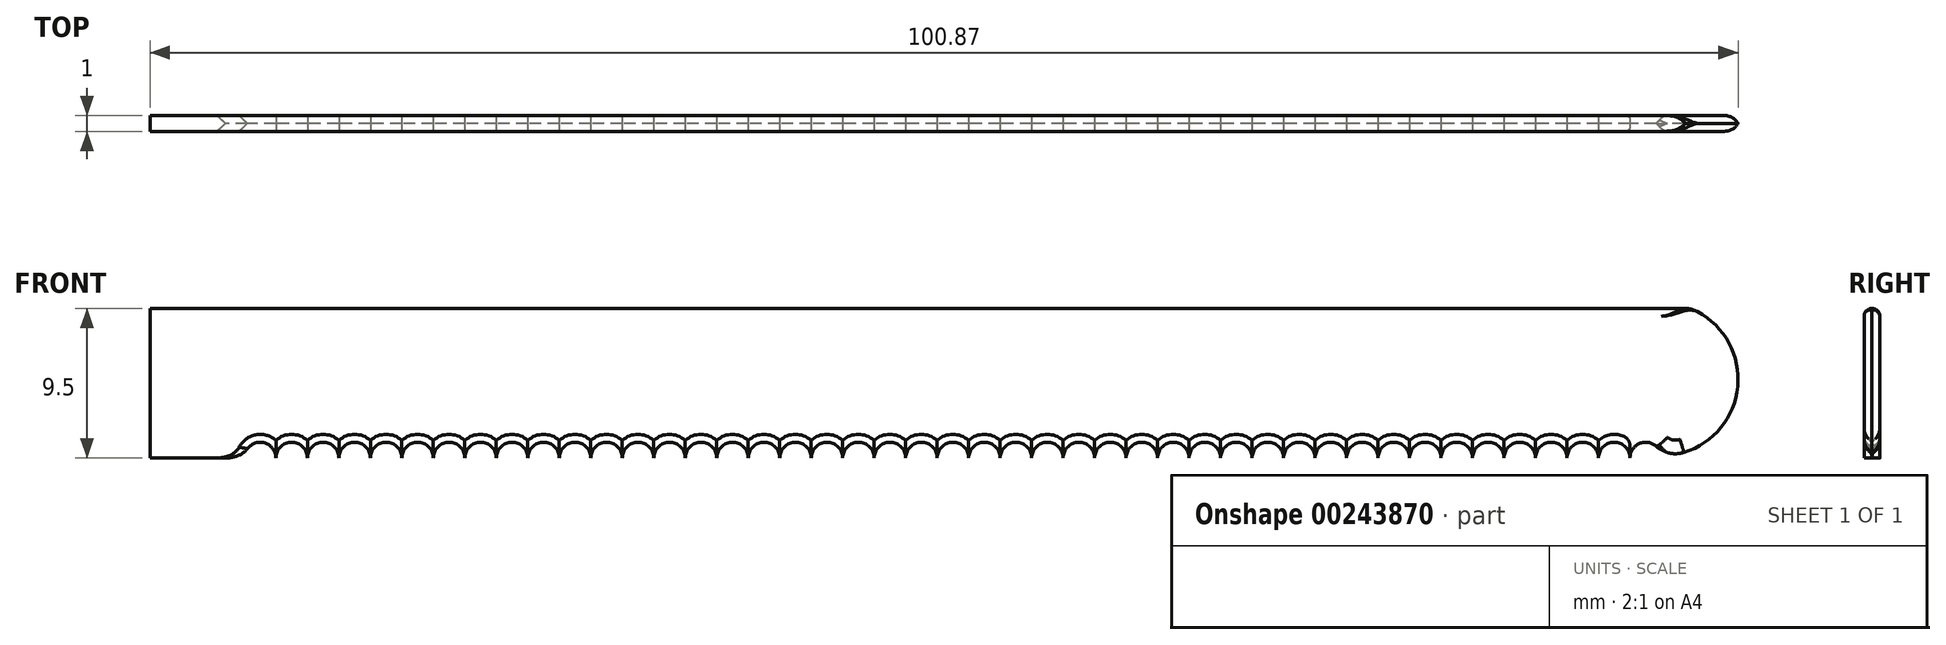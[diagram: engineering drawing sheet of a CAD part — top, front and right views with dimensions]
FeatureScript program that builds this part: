
annotation { "Feature Type Name" : "Feature", "Feature Type Description" : "" }
export const myFeature = defineFeature(function(context is Context, id is Id, definition is map)
    precondition{}
    {
        {
            var Q0;
            Q0=qCreatedBy(makeId("Front.planeOp"),FACE);
            var sketch = newSketch(context, id + "F0", { "sketchPlane" : qUnion([Q0])});
            skLineSegment(sketch, "E0.top", {"start": v(30, 10) * mm, "end": v(-60, 10) * mm});
            skLineSegment(sketch, "E0.right", {"start": v(-60, 0) * mm, "end": v(-60, 10) * mm});
            skLineSegment(sketch, "E1", {"start": v(-60, 0) * mm, "end": v(-58, 0) * mm});
            skLineSegment(sketch, "E2", {"start": v(-58, 0) * mm, "end": v(-56, 0) * mm});
            skLineSegment(sketch, "E3", {"start": v(-56, 0) * mm, "end": v(-54, 0) * mm});
            skLineSegment(sketch, "E4.bottom", {"start": v(-60, 10) * mm, "end": v(-66, 10) * mm});
            skLineSegment(sketch, "E4.top", {"start": v(-60, 0) * mm, "end": v(-66, 0) * mm});
            skLineSegment(sketch, "E4.left", {"start": v(-60, 10) * mm, "end": v(-60, 0) * mm});
            skLineSegment(sketch, "E4.right", {"start": v(-66, 10) * mm, "end": v(-66, 0) * mm});
            skArc(sketch, "E5", {"start": v(-58, 0) * mm, "mid": v(-59, 1) * mm, "end": v(-60, 0) * mm});
            skArc(sketch, "E6", {"start": v(-56, 0) * mm, "mid": v(-57, 1) * mm, "end": v(-58, 0) * mm});
            skArc(sketch, "E7", {"start": v(-54, 0) * mm, "mid": v(-55, 1) * mm, "end": v(-56, 0) * mm});
            skLineSegment(sketch, "E8", {"start": v(-54, 0) * mm, "end": v(-52, 0) * mm});
            skLineSegment(sketch, "E9", {"start": v(-52, 0) * mm, "end": v(-50, 0) * mm});
            skLineSegment(sketch, "E10", {"start": v(-50, 0) * mm, "end": v(-48, 0) * mm});
            skLineSegment(sketch, "E11", {"start": v(-48, 0) * mm, "end": v(-46, 0) * mm});
            skLineSegment(sketch, "E12", {"start": v(-46, 0) * mm, "end": v(-44, 0) * mm});
            skLineSegment(sketch, "E13", {"start": v(-44, 0) * mm, "end": v(-42, 0) * mm});
            skLineSegment(sketch, "E14", {"start": v(-42, 0) * mm, "end": v(-40, 0) * mm});
            skLineSegment(sketch, "E15", {"start": v(-40, 0) * mm, "end": v(-38, 0) * mm});
            skLineSegment(sketch, "E16", {"start": v(-38, 0) * mm, "end": v(-36, 0) * mm});
            skLineSegment(sketch, "E17", {"start": v(-36, 0) * mm, "end": v(-34, 0) * mm});
            skLineSegment(sketch, "E18", {"start": v(-34, 0) * mm, "end": v(-32, 0) * mm});
            skLineSegment(sketch, "E19", {"start": v(-32, 0) * mm, "end": v(-30, 0) * mm});
            skLineSegment(sketch, "E20", {"start": v(-30, 0) * mm, "end": v(-28, 0) * mm});
            skLineSegment(sketch, "E21", {"start": v(-28, 0) * mm, "end": v(-26, 0) * mm});
            skLineSegment(sketch, "E22", {"start": v(-26, 0) * mm, "end": v(-24, 0) * mm});
            skLineSegment(sketch, "E23", {"start": v(-24, 0) * mm, "end": v(-22, 0) * mm});
            skLineSegment(sketch, "E24", {"start": v(-22, 0) * mm, "end": v(-20, 0) * mm});
            skLineSegment(sketch, "E25", {"start": v(-20, 0) * mm, "end": v(-18, 0) * mm});
            skLineSegment(sketch, "E26", {"start": v(-18, 0) * mm, "end": v(-16, 0) * mm});
            skLineSegment(sketch, "E27", {"start": v(-16, 0) * mm, "end": v(-14, 0) * mm});
            skLineSegment(sketch, "E28", {"start": v(-14, 0) * mm, "end": v(-12, 0) * mm});
            skLineSegment(sketch, "E29", {"start": v(-12, 0) * mm, "end": v(-10, 0) * mm});
            skLineSegment(sketch, "E30", {"start": v(-10, 0) * mm, "end": v(-8, 0) * mm});
            skLineSegment(sketch, "E31", {"start": v(-8, 0) * mm, "end": v(-6, 0) * mm});
            skLineSegment(sketch, "E32", {"start": v(-6, 0) * mm, "end": v(-4, 0) * mm});
            skLineSegment(sketch, "E33", {"start": v(-4, 0) * mm, "end": v(-2, 0) * mm});
            skLineSegment(sketch, "E34", {"start": v(-2, 0) * mm, "end": v(0, 0) * mm});
            skArc(sketch, "E35", {"start": v(-52, 0) * mm, "mid": v(-53, 1) * mm, "end": v(-54, 0) * mm});
            skArc(sketch, "E36", {"start": v(-50, 0) * mm, "mid": v(-51, 1) * mm, "end": v(-52, 0) * mm});
            skArc(sketch, "E37", {"start": v(-48, 0) * mm, "mid": v(-49, 1) * mm, "end": v(-50, 0) * mm});
            skArc(sketch, "E38", {"start": v(-46, 0) * mm, "mid": v(-47, 1) * mm, "end": v(-48, 0) * mm});
            skArc(sketch, "E39", {"start": v(-44, 0) * mm, "mid": v(-45, 1) * mm, "end": v(-46, 0) * mm});
            skArc(sketch, "E40", {"start": v(-42, 0) * mm, "mid": v(-43, 1) * mm, "end": v(-44, 0) * mm});
            skArc(sketch, "E41", {"start": v(-40, 0) * mm, "mid": v(-41, 1) * mm, "end": v(-42, 0) * mm});
            skArc(sketch, "E42", {"start": v(-38, 0) * mm, "mid": v(-39, 1) * mm, "end": v(-40, 0) * mm});
            skArc(sketch, "E43", {"start": v(-36, 0) * mm, "mid": v(-37, 1) * mm, "end": v(-38, 0) * mm});
            skArc(sketch, "E44", {"start": v(-34, 0) * mm, "mid": v(-35, 1) * mm, "end": v(-36, 0) * mm});
            skArc(sketch, "E45", {"start": v(-32, 0) * mm, "mid": v(-33, 1) * mm, "end": v(-34, 0) * mm});
            skArc(sketch, "E46", {"start": v(-30, 0) * mm, "mid": v(-31, 1) * mm, "end": v(-32, 0) * mm});
            skArc(sketch, "E47", {"start": v(-28, 0) * mm, "mid": v(-29, 1) * mm, "end": v(-30, 0) * mm});
            skArc(sketch, "E48", {"start": v(-26, 0) * mm, "mid": v(-27, 1) * mm, "end": v(-28, 0) * mm});
            skArc(sketch, "E49", {"start": v(-24, 0) * mm, "mid": v(-25, 1) * mm, "end": v(-26, 0) * mm});
            skArc(sketch, "E50", {"start": v(-22, 0) * mm, "mid": v(-23, 1) * mm, "end": v(-24, 0) * mm});
            skArc(sketch, "E51", {"start": v(-20, 0) * mm, "mid": v(-21, 1) * mm, "end": v(-22, 0) * mm});
            skArc(sketch, "E52", {"start": v(-18, 0) * mm, "mid": v(-19, 1) * mm, "end": v(-20, 0) * mm});
            skArc(sketch, "E53", {"start": v(-16, 0) * mm, "mid": v(-17, 1) * mm, "end": v(-18, 0) * mm});
            skArc(sketch, "E54", {"start": v(-14, 0) * mm, "mid": v(-15, 1) * mm, "end": v(-16, 0) * mm});
            skArc(sketch, "E55", {"start": v(-12, 0) * mm, "mid": v(-13, 1) * mm, "end": v(-14, 0) * mm});
            skArc(sketch, "E56", {"start": v(-10, 0) * mm, "mid": v(-11, 1) * mm, "end": v(-12, 0) * mm});
            skArc(sketch, "E57", {"start": v(-8, 0) * mm, "mid": v(-9, 1) * mm, "end": v(-10, 0) * mm});
            skArc(sketch, "E58", {"start": v(-6, 0) * mm, "mid": v(-7, 1) * mm, "end": v(-8, 0) * mm});
            skArc(sketch, "E59", {"start": v(-4, 0) * mm, "mid": v(-5, 1) * mm, "end": v(-6, 0) * mm});
            skArc(sketch, "E60", {"start": v(-2, 0) * mm, "mid": v(-3, 1) * mm, "end": v(-4, 0) * mm});
            skArc(sketch, "E61", {"start": v(0, 0) * mm, "mid": v(-1, 1) * mm, "end": v(-2, 0) * mm});
            skLineSegment(sketch, "E62", {"start": v(30, 10) * mm, "end": v(30, 0) * mm});
            skLineSegment(sketch, "E63", {"start": v(0, 0) * mm, "end": v(2, 0) * mm});
            skLineSegment(sketch, "E64", {"start": v(2, 0) * mm, "end": v(4, 0) * mm});
            skLineSegment(sketch, "E65", {"start": v(4, 0) * mm, "end": v(6, 0) * mm});
            skLineSegment(sketch, "E66", {"start": v(6, 0) * mm, "end": v(8, 0) * mm});
            skLineSegment(sketch, "E67", {"start": v(8, 0) * mm, "end": v(10, 0) * mm});
            skLineSegment(sketch, "E68", {"start": v(10, 0) * mm, "end": v(12, 0) * mm});
            skLineSegment(sketch, "E69", {"start": v(12, 0) * mm, "end": v(14, 0) * mm});
            skLineSegment(sketch, "E70", {"start": v(14, 0) * mm, "end": v(16, 0) * mm});
            skLineSegment(sketch, "E71", {"start": v(16, 0) * mm, "end": v(18, 0) * mm});
            skLineSegment(sketch, "E72", {"start": v(18, 0) * mm, "end": v(20, 0) * mm});
            skLineSegment(sketch, "E73", {"start": v(20, 0) * mm, "end": v(22, 0) * mm});
            skLineSegment(sketch, "E74", {"start": v(22, 0) * mm, "end": v(24, 0) * mm});
            skLineSegment(sketch, "E75", {"start": v(24, 0) * mm, "end": v(26, 0) * mm});
            skLineSegment(sketch, "E76", {"start": v(26, 0) * mm, "end": v(28, 0) * mm});
            skLineSegment(sketch, "E77", {"start": v(28, 0) * mm, "end": v(30, 0) * mm});
            skArc(sketch, "E78", {"start": v(2, 0) * mm, "mid": v(1, 1) * mm, "end": v(0, 0) * mm});
            skArc(sketch, "E79", {"start": v(4, 0) * mm, "mid": v(3, 1) * mm, "end": v(2, 0) * mm});
            skArc(sketch, "E80", {"start": v(6, 0) * mm, "mid": v(5, 1) * mm, "end": v(4, 0) * mm});
            skArc(sketch, "E81", {"start": v(8, 0) * mm, "mid": v(7, 1) * mm, "end": v(6, 0) * mm});
            skArc(sketch, "E82", {"start": v(10, 0) * mm, "mid": v(9, 1) * mm, "end": v(8, 0) * mm});
            skArc(sketch, "E83", {"start": v(12, 0) * mm, "mid": v(11, 1) * mm, "end": v(10, 0) * mm});
            skArc(sketch, "E84", {"start": v(14, 0) * mm, "mid": v(13, 1) * mm, "end": v(12, 0) * mm});
            skArc(sketch, "E85", {"start": v(16, 0) * mm, "mid": v(15, 1) * mm, "end": v(14, 0) * mm});
            skArc(sketch, "E86", {"start": v(18, 0) * mm, "mid": v(17, 1) * mm, "end": v(16, 0) * mm});
            skArc(sketch, "E87", {"start": v(20, 0) * mm, "mid": v(19, 1) * mm, "end": v(18, 0) * mm});
            skArc(sketch, "E88", {"start": v(22, 0) * mm, "mid": v(21, 1) * mm, "end": v(20, 0) * mm});
            skArc(sketch, "E89", {"start": v(24, 0) * mm, "mid": v(23, 1) * mm, "end": v(22, 0) * mm});
            skArc(sketch, "E90", {"start": v(26, 0) * mm, "mid": v(25, 1) * mm, "end": v(24, 0) * mm});
            skArc(sketch, "E91", {"start": v(28, 0) * mm, "mid": v(27, 1) * mm, "end": v(26, 0) * mm});
            skArc(sketch, "E92", {"start": v(30, 0) * mm, "mid": v(29, 1) * mm, "end": v(28, 0) * mm});
            skArc(sketch, "E93", {"start": v(30, 0) * mm, "mid": v(35, 5) * mm, "end": v(30, 10) * mm});
            skSolve(sketch);
        }
        {
            var Q0;
            Q0=makeQuery(id+"F0.imprint","IMPRINT",FACE,{"disambiguationData":[TD([[makeQuery(id+"F0.imprint","IMPRINT",EDGE,{"derivedFrom":sQuery(id+"F0.wireOp",EDGE,"E4.bottom")}),1.0]])]});
            var Q1;
            Q1=makeQuery(id+"F0.imprint","IMPRINT",FACE,{"disambiguationData":[TD([[makeQuery(id+"F0.imprint","IMPRINT",EDGE,{"derivedFrom":sQuery(id+"F0.wireOp",EDGE,"E0.top")}),1.0]])]});
            var Q2;
            Q2=makeQuery(id+"F0.imprint","IMPRINT",FACE,{"disambiguationData":[TD([[makeQuery(id+"F0.imprint","IMPRINT",EDGE,{"derivedFrom":sQuery(id+"F0.wireOp",EDGE,"E62")}),1.0]])]});
            extrude(context, id + "F1", {"entities" : qUnion([Q0, Q1, Q2]), "depth" : 1 * mm});
        }
        {
            var Q0;
            Q0=makeQuery(id+"F1.opExtrude","CAP_EDGE",EDGE,{"disambiguationData":[OSD([sQuery(id+"F0.wireOp",EDGE,"E53")])],"isStart":true});
            var Q1;
            Q1=makeQuery(id+"F1.opExtrude","CAP_EDGE",EDGE,{"disambiguationData":[OSD([sQuery(id+"F0.wireOp",EDGE,"E53")])],"isStart":false});
            var Q2;
            Q2=makeQuery(id+"F1.opExtrude","CAP_EDGE",EDGE,{"disambiguationData":[OSD([sQuery(id+"F0.wireOp",EDGE,"E5")])],"isStart":true});
            var Q3;
            Q3=makeQuery(id+"F1.opExtrude","CAP_EDGE",EDGE,{"disambiguationData":[OSD([sQuery(id+"F0.wireOp",EDGE,"E5")])],"isStart":false});
            var Q4;
            Q4=makeQuery(id+"F1.opExtrude","CAP_EDGE",EDGE,{"disambiguationData":[OSD([sQuery(id+"F0.wireOp",EDGE,"E6")])],"isStart":false});
            var Q5;
            Q5=makeQuery(id+"F1.opExtrude","CAP_EDGE",EDGE,{"disambiguationData":[OSD([sQuery(id+"F0.wireOp",EDGE,"E6")])],"isStart":true});
            var Q6;
            Q6=makeQuery(id+"F1.opExtrude","CAP_EDGE",EDGE,{"disambiguationData":[OSD([sQuery(id+"F0.wireOp",EDGE,"E7")])],"isStart":true});
            var Q7;
            Q7=makeQuery(id+"F1.opExtrude","CAP_EDGE",EDGE,{"disambiguationData":[OSD([sQuery(id+"F0.wireOp",EDGE,"E7")])],"isStart":false});
            var Q8;
            Q8=makeQuery(id+"F1.opExtrude","CAP_EDGE",EDGE,{"disambiguationData":[OSD([sQuery(id+"F0.wireOp",EDGE,"E35")])],"isStart":false});
            var Q9;
            Q9=makeQuery(id+"F1.opExtrude","CAP_EDGE",EDGE,{"disambiguationData":[OSD([sQuery(id+"F0.wireOp",EDGE,"E35")])],"isStart":true});
            var Q10;
            Q10=makeQuery(id+"F1.opExtrude","CAP_EDGE",EDGE,{"disambiguationData":[OSD([sQuery(id+"F0.wireOp",EDGE,"E36")])],"isStart":false});
            var Q11;
            Q11=makeQuery(id+"F1.opExtrude","CAP_EDGE",EDGE,{"disambiguationData":[OSD([sQuery(id+"F0.wireOp",EDGE,"E36")])],"isStart":true});
            var Q12;
            Q12=makeQuery(id+"F1.opExtrude","CAP_EDGE",EDGE,{"disambiguationData":[OSD([sQuery(id+"F0.wireOp",EDGE,"E37")])],"isStart":false});
            var Q13;
            Q13=makeQuery(id+"F1.opExtrude","CAP_EDGE",EDGE,{"disambiguationData":[OSD([sQuery(id+"F0.wireOp",EDGE,"E37")])],"isStart":true});
            var Q14;
            Q14=makeQuery(id+"F1.opExtrude","CAP_EDGE",EDGE,{"disambiguationData":[OSD([sQuery(id+"F0.wireOp",EDGE,"E38")])],"isStart":false});
            var Q15;
            Q15=makeQuery(id+"F1.opExtrude","CAP_EDGE",EDGE,{"disambiguationData":[OSD([sQuery(id+"F0.wireOp",EDGE,"E38")])],"isStart":true});
            var Q16;
            Q16=makeQuery(id+"F1.opExtrude","CAP_EDGE",EDGE,{"disambiguationData":[OSD([sQuery(id+"F0.wireOp",EDGE,"E39")])],"isStart":false});
            var Q17;
            Q17=makeQuery(id+"F1.opExtrude","CAP_EDGE",EDGE,{"disambiguationData":[OSD([sQuery(id+"F0.wireOp",EDGE,"E39")])],"isStart":true});
            var Q18;
            Q18=makeQuery(id+"F1.opExtrude","CAP_EDGE",EDGE,{"disambiguationData":[OSD([sQuery(id+"F0.wireOp",EDGE,"E40")])],"isStart":false});
            var Q19;
            Q19=makeQuery(id+"F1.opExtrude","CAP_EDGE",EDGE,{"disambiguationData":[OSD([sQuery(id+"F0.wireOp",EDGE,"E40")])],"isStart":true});
            var Q20;
            Q20=makeQuery(id+"F1.opExtrude","CAP_EDGE",EDGE,{"disambiguationData":[OSD([sQuery(id+"F0.wireOp",EDGE,"E41")])],"isStart":false});
            var Q21;
            Q21=makeQuery(id+"F1.opExtrude","CAP_EDGE",EDGE,{"disambiguationData":[OSD([sQuery(id+"F0.wireOp",EDGE,"E41")])],"isStart":true});
            var Q22;
            Q22=makeQuery(id+"F1.opExtrude","CAP_EDGE",EDGE,{"disambiguationData":[OSD([sQuery(id+"F0.wireOp",EDGE,"E42")])],"isStart":false});
            var Q23;
            Q23=makeQuery(id+"F1.opExtrude","CAP_EDGE",EDGE,{"disambiguationData":[OSD([sQuery(id+"F0.wireOp",EDGE,"E42")])],"isStart":true});
            var Q24;
            Q24=makeQuery(id+"F1.opExtrude","CAP_EDGE",EDGE,{"disambiguationData":[OSD([sQuery(id+"F0.wireOp",EDGE,"E43")])],"isStart":false});
            var Q25;
            Q25=makeQuery(id+"F1.opExtrude","CAP_EDGE",EDGE,{"disambiguationData":[OSD([sQuery(id+"F0.wireOp",EDGE,"E43")])],"isStart":true});
            var Q26;
            Q26=makeQuery(id+"F1.opExtrude","CAP_EDGE",EDGE,{"disambiguationData":[OSD([sQuery(id+"F0.wireOp",EDGE,"E44")])],"isStart":false});
            var Q27;
            Q27=makeQuery(id+"F1.opExtrude","CAP_EDGE",EDGE,{"disambiguationData":[OSD([sQuery(id+"F0.wireOp",EDGE,"E44")])],"isStart":true});
            var Q28;
            Q28=makeQuery(id+"F1.opExtrude","CAP_EDGE",EDGE,{"disambiguationData":[OSD([sQuery(id+"F0.wireOp",EDGE,"E45")])],"isStart":false});
            var Q29;
            Q29=makeQuery(id+"F1.opExtrude","CAP_EDGE",EDGE,{"disambiguationData":[OSD([sQuery(id+"F0.wireOp",EDGE,"E45")])],"isStart":true});
            var Q30;
            Q30=makeQuery(id+"F1.opExtrude","CAP_EDGE",EDGE,{"disambiguationData":[OSD([sQuery(id+"F0.wireOp",EDGE,"E46")])],"isStart":false});
            var Q31;
            Q31=makeQuery(id+"F1.opExtrude","CAP_EDGE",EDGE,{"disambiguationData":[OSD([sQuery(id+"F0.wireOp",EDGE,"E46")])],"isStart":true});
            var Q32;
            Q32=makeQuery(id+"F1.opExtrude","CAP_EDGE",EDGE,{"disambiguationData":[OSD([sQuery(id+"F0.wireOp",EDGE,"E47")])],"isStart":false});
            var Q33;
            Q33=makeQuery(id+"F1.opExtrude","CAP_EDGE",EDGE,{"disambiguationData":[OSD([sQuery(id+"F0.wireOp",EDGE,"E47")])],"isStart":true});
            var Q34;
            Q34=makeQuery(id+"F1.opExtrude","CAP_EDGE",EDGE,{"disambiguationData":[OSD([sQuery(id+"F0.wireOp",EDGE,"E48")])],"isStart":false});
            var Q35;
            Q35=makeQuery(id+"F1.opExtrude","CAP_EDGE",EDGE,{"disambiguationData":[OSD([sQuery(id+"F0.wireOp",EDGE,"E48")])],"isStart":true});
            var Q36;
            Q36=makeQuery(id+"F1.opExtrude","CAP_EDGE",EDGE,{"disambiguationData":[OSD([sQuery(id+"F0.wireOp",EDGE,"E49")])],"isStart":false});
            var Q37;
            Q37=makeQuery(id+"F1.opExtrude","CAP_EDGE",EDGE,{"disambiguationData":[OSD([sQuery(id+"F0.wireOp",EDGE,"E49")])],"isStart":true});
            var Q38;
            Q38=makeQuery(id+"F1.opExtrude","CAP_EDGE",EDGE,{"disambiguationData":[OSD([sQuery(id+"F0.wireOp",EDGE,"E50")])],"isStart":false});
            var Q39;
            Q39=makeQuery(id+"F1.opExtrude","CAP_EDGE",EDGE,{"disambiguationData":[OSD([sQuery(id+"F0.wireOp",EDGE,"E50")])],"isStart":true});
            var Q40;
            Q40=makeQuery(id+"F1.opExtrude","CAP_EDGE",EDGE,{"disambiguationData":[OSD([sQuery(id+"F0.wireOp",EDGE,"E51")])],"isStart":false});
            var Q41;
            Q41=makeQuery(id+"F1.opExtrude","CAP_EDGE",EDGE,{"disambiguationData":[OSD([sQuery(id+"F0.wireOp",EDGE,"E51")])],"isStart":true});
            var Q42;
            Q42=makeQuery(id+"F1.opExtrude","CAP_EDGE",EDGE,{"disambiguationData":[OSD([sQuery(id+"F0.wireOp",EDGE,"E52")])],"isStart":false});
            var Q43;
            Q43=makeQuery(id+"F1.opExtrude","CAP_EDGE",EDGE,{"disambiguationData":[OSD([sQuery(id+"F0.wireOp",EDGE,"E52")])],"isStart":true});
            var Q44;
            Q44=makeQuery(id+"F1.opExtrude","CAP_EDGE",EDGE,{"disambiguationData":[OSD([sQuery(id+"F0.wireOp",EDGE,"E54")])],"isStart":false});
            var Q45;
            Q45=makeQuery(id+"F1.opExtrude","CAP_EDGE",EDGE,{"disambiguationData":[OSD([sQuery(id+"F0.wireOp",EDGE,"E54")])],"isStart":true});
            var Q46;
            Q46=makeQuery(id+"F1.opExtrude","CAP_EDGE",EDGE,{"disambiguationData":[OSD([sQuery(id+"F0.wireOp",EDGE,"E55")])],"isStart":false});
            var Q47;
            Q47=makeQuery(id+"F1.opExtrude","CAP_EDGE",EDGE,{"disambiguationData":[OSD([sQuery(id+"F0.wireOp",EDGE,"E55")])],"isStart":true});
            var Q48;
            Q48=makeQuery(id+"F1.opExtrude","CAP_EDGE",EDGE,{"disambiguationData":[OSD([sQuery(id+"F0.wireOp",EDGE,"E56")])],"isStart":false});
            var Q49;
            Q49=makeQuery(id+"F1.opExtrude","CAP_EDGE",EDGE,{"disambiguationData":[OSD([sQuery(id+"F0.wireOp",EDGE,"E56")])],"isStart":true});
            var Q50;
            Q50=makeQuery(id+"F1.opExtrude","CAP_EDGE",EDGE,{"disambiguationData":[OSD([sQuery(id+"F0.wireOp",EDGE,"E57")])],"isStart":false});
            var Q51;
            Q51=makeQuery(id+"F1.opExtrude","CAP_EDGE",EDGE,{"disambiguationData":[OSD([sQuery(id+"F0.wireOp",EDGE,"E57")])],"isStart":true});
            var Q52;
            Q52=makeQuery(id+"F1.opExtrude","CAP_EDGE",EDGE,{"disambiguationData":[OSD([sQuery(id+"F0.wireOp",EDGE,"E58")])],"isStart":false});
            var Q53;
            Q53=makeQuery(id+"F1.opExtrude","CAP_EDGE",EDGE,{"disambiguationData":[OSD([sQuery(id+"F0.wireOp",EDGE,"E58")])],"isStart":true});
            var Q54;
            Q54=makeQuery(id+"F1.opExtrude","CAP_EDGE",EDGE,{"disambiguationData":[OSD([sQuery(id+"F0.wireOp",EDGE,"E59")])],"isStart":false});
            var Q55;
            Q55=makeQuery(id+"F1.opExtrude","CAP_EDGE",EDGE,{"disambiguationData":[OSD([sQuery(id+"F0.wireOp",EDGE,"E59")])],"isStart":true});
            var Q56;
            Q56=makeQuery(id+"F1.opExtrude","CAP_EDGE",EDGE,{"disambiguationData":[OSD([sQuery(id+"F0.wireOp",EDGE,"E60")])],"isStart":false});
            var Q57;
            Q57=makeQuery(id+"F1.opExtrude","CAP_EDGE",EDGE,{"disambiguationData":[OSD([sQuery(id+"F0.wireOp",EDGE,"E60")])],"isStart":true});
            var Q58;
            Q58=makeQuery(id+"F1.opExtrude","CAP_EDGE",EDGE,{"disambiguationData":[OSD([sQuery(id+"F0.wireOp",EDGE,"E61")])],"isStart":false});
            var Q59;
            Q59=makeQuery(id+"F1.opExtrude","CAP_EDGE",EDGE,{"disambiguationData":[OSD([sQuery(id+"F0.wireOp",EDGE,"E61")])],"isStart":true});
            var Q60;
            Q60=makeQuery(id+"F1.opExtrude","CAP_EDGE",EDGE,{"disambiguationData":[OSD([sQuery(id+"F0.wireOp",EDGE,"SpO6Y4JU-sQG2-NbLW-cU8e-jWpR7E6E2uC7")])],"isStart":true});
            var Q61;
            Q61=makeQuery(id+"F1.opExtrude","CAP_EDGE",EDGE,{"disambiguationData":[OSD([sQuery(id+"F0.wireOp",EDGE,"SpO6Y4JU-sQG2-NbLW-cU8e-jWpR7E6E2uC7")])],"isStart":false});
            var Q62;
            Q62=makeQuery(id+"F1.opExtrude","CAP_EDGE",EDGE,{"disambiguationData":[OSD([sQuery(id+"F0.wireOp",EDGE,"E78")])],"isStart":false});
            var Q63;
            Q63=makeQuery(id+"F1.opExtrude","CAP_EDGE",EDGE,{"disambiguationData":[OSD([sQuery(id+"F0.wireOp",EDGE,"E78")])],"isStart":true});
            var Q64;
            Q64=makeQuery(id+"F1.opExtrude","CAP_EDGE",EDGE,{"disambiguationData":[OSD([sQuery(id+"F0.wireOp",EDGE,"E79")])],"isStart":false});
            var Q65;
            Q65=makeQuery(id+"F1.opExtrude","CAP_EDGE",EDGE,{"disambiguationData":[OSD([sQuery(id+"F0.wireOp",EDGE,"E79")])],"isStart":true});
            var Q66;
            Q66=makeQuery(id+"F1.opExtrude","CAP_EDGE",EDGE,{"disambiguationData":[OSD([sQuery(id+"F0.wireOp",EDGE,"E80")])],"isStart":false});
            var Q67;
            Q67=makeQuery(id+"F1.opExtrude","CAP_EDGE",EDGE,{"disambiguationData":[OSD([sQuery(id+"F0.wireOp",EDGE,"E80")])],"isStart":true});
            var Q68;
            Q68=makeQuery(id+"F1.opExtrude","CAP_EDGE",EDGE,{"disambiguationData":[OSD([sQuery(id+"F0.wireOp",EDGE,"E81")])],"isStart":false});
            var Q69;
            Q69=makeQuery(id+"F1.opExtrude","CAP_EDGE",EDGE,{"disambiguationData":[OSD([sQuery(id+"F0.wireOp",EDGE,"E81")])],"isStart":true});
            var Q70;
            Q70=makeQuery(id+"F1.opExtrude","CAP_EDGE",EDGE,{"disambiguationData":[OSD([sQuery(id+"F0.wireOp",EDGE,"E82")])],"isStart":false});
            var Q71;
            Q71=makeQuery(id+"F1.opExtrude","CAP_EDGE",EDGE,{"disambiguationData":[OSD([sQuery(id+"F0.wireOp",EDGE,"E82")])],"isStart":true});
            var Q72;
            Q72=makeQuery(id+"F1.opExtrude","CAP_EDGE",EDGE,{"disambiguationData":[OSD([sQuery(id+"F0.wireOp",EDGE,"E83")])],"isStart":false});
            var Q73;
            Q73=makeQuery(id+"F1.opExtrude","CAP_EDGE",EDGE,{"disambiguationData":[OSD([sQuery(id+"F0.wireOp",EDGE,"E83")])],"isStart":true});
            var Q74;
            Q74=makeQuery(id+"F1.opExtrude","CAP_EDGE",EDGE,{"disambiguationData":[OSD([sQuery(id+"F0.wireOp",EDGE,"E84")])],"isStart":false});
            var Q75;
            Q75=makeQuery(id+"F1.opExtrude","CAP_EDGE",EDGE,{"disambiguationData":[OSD([sQuery(id+"F0.wireOp",EDGE,"E84")])],"isStart":true});
            var Q76;
            Q76=makeQuery(id+"F1.opExtrude","CAP_EDGE",EDGE,{"disambiguationData":[OSD([sQuery(id+"F0.wireOp",EDGE,"E85")])],"isStart":false});
            var Q77;
            Q77=makeQuery(id+"F1.opExtrude","CAP_EDGE",EDGE,{"disambiguationData":[OSD([sQuery(id+"F0.wireOp",EDGE,"E85")])],"isStart":true});
            var Q78;
            Q78=makeQuery(id+"F1.opExtrude","CAP_EDGE",EDGE,{"disambiguationData":[OSD([sQuery(id+"F0.wireOp",EDGE,"E86")])],"isStart":false});
            var Q79;
            Q79=makeQuery(id+"F1.opExtrude","CAP_EDGE",EDGE,{"disambiguationData":[OSD([sQuery(id+"F0.wireOp",EDGE,"E86")])],"isStart":true});
            var Q80;
            Q80=makeQuery(id+"F1.opExtrude","CAP_EDGE",EDGE,{"disambiguationData":[OSD([sQuery(id+"F0.wireOp",EDGE,"E87")])],"isStart":false});
            var Q81;
            Q81=makeQuery(id+"F1.opExtrude","CAP_EDGE",EDGE,{"disambiguationData":[OSD([sQuery(id+"F0.wireOp",EDGE,"E87")])],"isStart":true});
            var Q82;
            Q82=makeQuery(id+"F1.opExtrude","CAP_EDGE",EDGE,{"disambiguationData":[OSD([sQuery(id+"F0.wireOp",EDGE,"E88")])],"isStart":false});
            var Q83;
            Q83=makeQuery(id+"F1.opExtrude","CAP_EDGE",EDGE,{"disambiguationData":[OSD([sQuery(id+"F0.wireOp",EDGE,"E88")])],"isStart":true});
            var Q84;
            Q84=makeQuery(id+"F1.opExtrude","CAP_EDGE",EDGE,{"disambiguationData":[OSD([sQuery(id+"F0.wireOp",EDGE,"E89")])],"isStart":false});
            var Q85;
            Q85=makeQuery(id+"F1.opExtrude","CAP_EDGE",EDGE,{"disambiguationData":[OSD([sQuery(id+"F0.wireOp",EDGE,"E89")])],"isStart":true});
            var Q86;
            Q86=makeQuery(id+"F1.opExtrude","CAP_EDGE",EDGE,{"disambiguationData":[OSD([sQuery(id+"F0.wireOp",EDGE,"E90")])],"isStart":false});
            var Q87;
            Q87=makeQuery(id+"F1.opExtrude","CAP_EDGE",EDGE,{"disambiguationData":[OSD([sQuery(id+"F0.wireOp",EDGE,"E90")])],"isStart":true});
            var Q88;
            Q88=makeQuery(id+"F1.opExtrude","CAP_EDGE",EDGE,{"disambiguationData":[OSD([sQuery(id+"F0.wireOp",EDGE,"E91")])],"isStart":false});
            var Q89;
            Q89=makeQuery(id+"F1.opExtrude","CAP_EDGE",EDGE,{"disambiguationData":[OSD([sQuery(id+"F0.wireOp",EDGE,"E91")])],"isStart":true});
            var Q90;
            Q90=makeQuery(id+"F1.opExtrude","CAP_EDGE",EDGE,{"disambiguationData":[OSD([sQuery(id+"F0.wireOp",EDGE,"E92")])],"isStart":false});
            var Q91;
            Q91=makeQuery(id+"F1.opExtrude","CAP_EDGE",EDGE,{"disambiguationData":[OSD([sQuery(id+"F0.wireOp",EDGE,"E92")])],"isStart":true});
            chamfer(context, id + "F2", {"entities" : qUnion([Q0, Q1, Q2, Q3, Q4, Q5, Q6, Q7, Q8, Q9, Q10, Q11, Q12, Q13, Q14, Q15, Q16, Q17, Q18, Q19, Q20, Q21, Q22, Q23, Q24, Q25, Q26, Q27, Q28, Q29, Q30, Q31, Q32, Q33, Q34, Q35, Q36, Q37, Q38, Q39, Q40, Q41, Q42, Q43, Q44, Q45, Q46, Q47, Q48, Q49, Q50, Q51, Q52, Q53, Q54, Q55, Q56, Q57, Q58, Q59, Q60, Q61, Q62, Q63, Q64, Q65, Q66, Q67, Q68, Q69, Q70, Q71, Q72, Q73, Q74, Q75, Q76, Q77, Q78, Q79, Q80, Q81, Q82, Q83, Q84, Q85, Q86, Q87, Q88, Q89, Q90, Q91]), "width" : 0.5 * mm, "tangentPropagation" : true});
        }
        {
            var Q0;
            Q0=makeQuery(id+"F2.opChamfer","BLEND_EDGE",EDGE,{"blendedFrom":[makeQuery(id+"F1.opExtrude","CAP_EDGE",EDGE,{"disambiguationData":[OSD([sQuery(id+"F0.wireOp",EDGE,"E92")])],"isStart":false}),makeQuery(id+"F1.opExtrude","SWEPT_FACE",FACE,{"disambiguationData":[OSD([sQuery(id+"F0.wireOp",EDGE,"E93")])]})],"blendedInto":[makeQuery(id+"F1.opExtrude","SWEPT_FACE",FACE,{"disambiguationData":[OSD([sQuery(id+"F0.wireOp",EDGE,"E93")])]})]});
            var Q1;
            Q1=makeQuery(id+"F2.opChamfer","BLEND_EDGE",EDGE,{"blendedFrom":[makeQuery(id+"F1.opExtrude","CAP_EDGE",EDGE,{"disambiguationData":[OSD([sQuery(id+"F0.wireOp",EDGE,"E92")])],"isStart":true}),makeQuery(id+"F1.opExtrude","SWEPT_FACE",FACE,{"disambiguationData":[OSD([sQuery(id+"F0.wireOp",EDGE,"E93")])]})],"blendedInto":[makeQuery(id+"F1.opExtrude","SWEPT_FACE",FACE,{"disambiguationData":[OSD([sQuery(id+"F0.wireOp",EDGE,"E93")])]})]});
            fillet(context, id + "F3", {"entities" : qUnion([Q0, Q1]), "radius" : 1.5 * mm, "tangentPropagation" : true, "allowEdgeOverflow" : false});
        }
        {
            var Q0;
            Q0=makeQuery(id+"F2.opChamfer","BLEND_EDGE",EDGE,{"blendedFrom":[makeQuery(id+"F1.opExtrude","CAP_EDGE",EDGE,{"disambiguationData":[OSD([sQuery(id+"F0.wireOp",EDGE,"E5")])],"isStart":true}),makeQuery(id+"F1.opExtrude","SWEPT_FACE",FACE,{"disambiguationData":[OSD([sQuery(id+"F0.wireOp",EDGE,"E4.top")])]})],"blendedInto":[makeQuery(id+"F1.opExtrude","SWEPT_FACE",FACE,{"disambiguationData":[OSD([sQuery(id+"F0.wireOp",EDGE,"E4.top")])]})]});
            var Q1;
            Q1=makeQuery(id+"F2.opChamfer","BLEND_EDGE",EDGE,{"blendedFrom":[makeQuery(id+"F1.opExtrude","CAP_EDGE",EDGE,{"disambiguationData":[OSD([sQuery(id+"F0.wireOp",EDGE,"E5")])],"isStart":false}),makeQuery(id+"F1.opExtrude","SWEPT_FACE",FACE,{"disambiguationData":[OSD([sQuery(id+"F0.wireOp",EDGE,"E4.top")])]})],"blendedInto":[makeQuery(id+"F1.opExtrude","SWEPT_FACE",FACE,{"disambiguationData":[OSD([sQuery(id+"F0.wireOp",EDGE,"E4.top")])]})]});
            fillet(context, id + "F4", {"entities" : qUnion([Q0, Q1]), "radius" : 1 * mm, "tangentPropagation" : true, "allowEdgeOverflow" : false});
        }
        {
            var Q0;
            Q0=makeQuery(id+"F1.opExtrude","CAP_EDGE",EDGE,{"disambiguationData":[OSD([sQuery(id+"F0.wireOp",EDGE,"E93")])],"isStart":false});
            var Q1;
            Q1=makeQuery(id+"F1.opExtrude","CAP_EDGE",EDGE,{"disambiguationData":[OSD([sQuery(id+"F0.wireOp",EDGE,"E93")])],"isStart":true});
            fillet(context, id + "F5", {"entities" : qUnion([Q0, Q1]), "radius" : 1 * mm, "tangentPropagation" : true, "allowEdgeOverflow" : false});
        }
        {
            var Q0;
            Q0=makeQuery(id+"F1.opExtrude","SWEPT_FACE",FACE,{"disambiguationData":[OSD([sQuery(id+"F0.wireOp",EDGE,"E4.right")])]});
            var sketch = newSketch(context, id + "F6", { "sketchPlane" : qUnion([Q0])});
            skArc(sketch, "E94", {"start": v(1, 9) * mm, "mid": v(0.5, 9.5) * mm, "end": v(0, 9) * mm});
            skLineSegment(sketch, "E95", {"start": v(0, 9) * mm, "end": v(1, 9) * mm});
            skSolve(sketch);
        }
        {
            var Q0;
            Q0=makeQuery(id+"F6.imprint","IMPRINT",FACE,{"disambiguationData":[TD([[makeQuery(id+"F6.imprint","IMPRINT",EDGE,{"derivedFrom":sQuery(id+"F6.wireOp",EDGE,"E94")}),-1.0]])]});
            extrude(context, id + "F7", {"entities" : qUnion([Q0]), "operationType" : NewBodyOperationType.REMOVE, "endBound" : BoundingType.THROUGH_ALL, "oppositeDirection" : true, "depth" : 25 * mm});
        }
        {
            var Q0;
            {var subQ0=sQuery(id+"F0.wireOp",EDGE,"E93");Q0=makeQuery(id+"F7.boolean.opBoolean","INTERSECT",EDGE,{"derivedFrom":[makeQuery(id+"F5.opFillet","BLEND_FACE",FACE,{"disambiguationData":[OSD([subQ0]),TDD([makeQuery(id+"F1.opExtrude","CAP_EDGE",EDGE,{"disambiguationData":[OSD([subQ0])],"isStart":false})])]}),makeQuery(id+"F7.opExtrude","SWEPT_FACE",FACE,{"disambiguationData":[OSD([sQuery(id+"F6.wireOp",EDGE,"E94")])]})]});}
            var Q1;
            {var subQ0=sQuery(id+"F0.wireOp",EDGE,"E93");Q1=makeQuery(id+"F7.boolean.opBoolean","INTERSECT",EDGE,{"derivedFrom":[makeQuery(id+"F5.opFillet","BLEND_FACE",FACE,{"disambiguationData":[OSD([subQ0]),TDD([makeQuery(id+"F1.opExtrude","CAP_EDGE",EDGE,{"disambiguationData":[OSD([subQ0])],"isStart":true})])]}),makeQuery(id+"F7.opExtrude","SWEPT_FACE",FACE,{"disambiguationData":[OSD([sQuery(id+"F6.wireOp",EDGE,"E94")])]})]});}
            fillet(context, id + "F8", {"entities" : qUnion([Q0, Q1]), "radius" : 0.33 * mm, "tangentPropagation" : true, "allowEdgeOverflow" : false});
        }
    });
